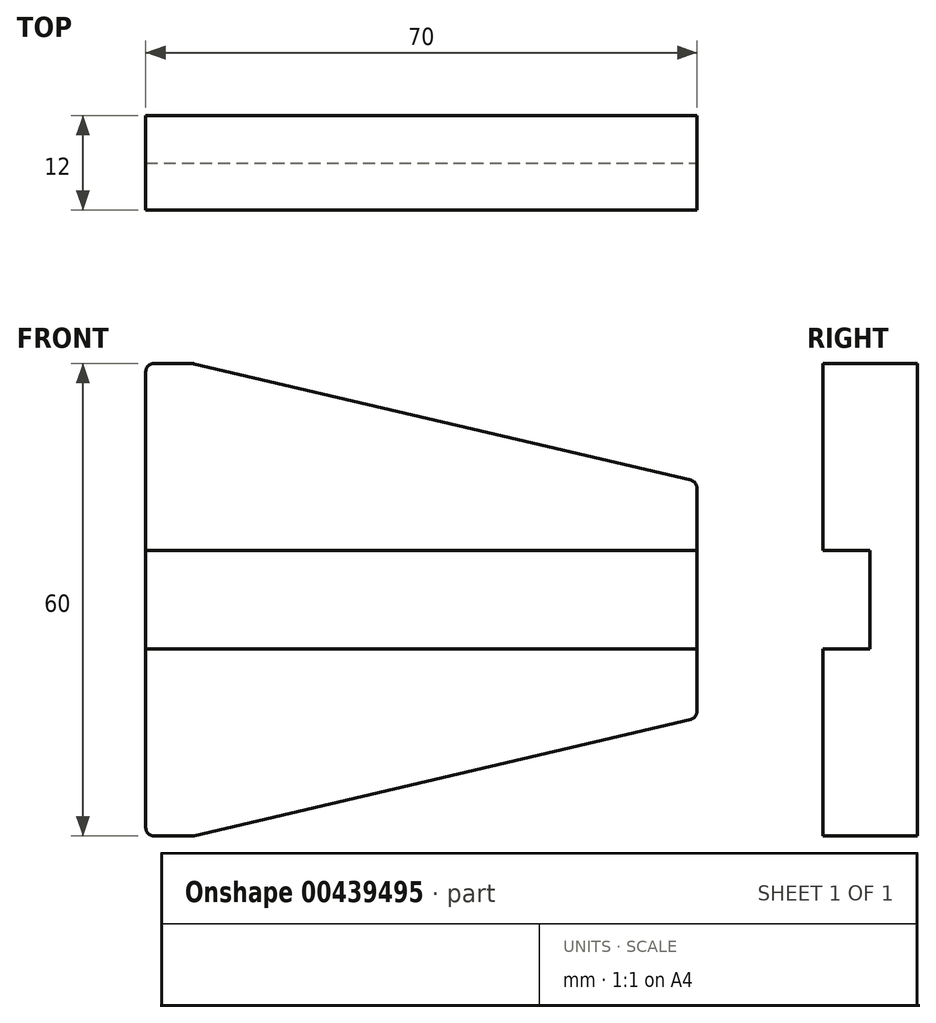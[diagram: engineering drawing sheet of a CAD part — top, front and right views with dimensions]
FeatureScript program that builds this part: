
annotation { "Feature Type Name" : "Feature", "Feature Type Description" : "" }
export const myFeature = defineFeature(function(context is Context, id is Id, definition is map)
    precondition{}
    {
        {
            var Q0;
            Q0=qCreatedBy(makeId("Front.planeOp"),FACE);
            var sketch = newSketch(context, id + "F0", { "sketchPlane" : qUnion([Q0])});
            skLineSegment(sketch, "E0", {"start": v(0, 30) * mm, "end": v(0, -30) * mm});
            skLineSegment(sketch, "E1", {"start": v(6, -30) * mm, "end": v(70, -15) * mm});
            skLineSegment(sketch, "E2", {"start": v(70, -15) * mm, "end": v(70, 15) * mm});
            skLineSegment(sketch, "E3", {"start": v(70, 15) * mm, "end": v(6, 30) * mm});
            skLineSegment(sketch, "E4", {"start": v(0, 30) * mm, "end": v(6, 30) * mm});
            skLineSegment(sketch, "E5", {"start": v(0, -30) * mm, "end": v(6, -30) * mm});
            skSolve(sketch);
        }
        {
            var Q0;
            Q0 = qSketchRegion(id + "F0", true);
            extrude(context, id + "F1", {"entities" : qUnion([Q0]), "depth" : 12 * mm, "offsetDistance" : 25 * mm});
        }
        {
            var Q0;
            Q0=makeQuery(id+"F1.opExtrude","SWEPT_FACE",FACE,{"disambiguationData":[OSD([sQuery(id+"F0.wireOp",EDGE,"E2")])]});
            var sketch = newSketch(context, id + "F2", { "sketchPlane" : qUnion([Q0])});
            skLineSegment(sketch, "E6.bottom", {"start": v(-12, 6.25) * mm, "end": v(-6, 6.25) * mm});
            skLineSegment(sketch, "E6.top", {"start": v(-12, -6.25) * mm, "end": v(-6, -6.25) * mm});
            skLineSegment(sketch, "E6.left", {"start": v(-12, 6.25) * mm, "end": v(-12, -6.25) * mm});
            skLineSegment(sketch, "E6.right", {"start": v(-6, 6.25) * mm, "end": v(-6, -6.25) * mm});
            skPoint(sketch, "E7", {"position": v(-12, 0) * mm});
            skPoint(sketch, "E7.positionSnap0", {"position": v(0, 0) * mm});
            skSolve(sketch);
        }
        {
            var Q0;
            Q0 = qSketchRegion(id + "F2", true);
            extrude(context, id + "F3", {"entities" : qUnion([Q0]), "operationType" : NewBodyOperationType.REMOVE, "endBound" : BoundingType.THROUGH_ALL, "oppositeDirection" : true, "depth" : 25 * mm, "offsetDistance" : 25 * mm});
        }
        {
            var Q0;
            Q0=makeQuery(id+"F1.opExtrude","SWEPT_EDGE",EDGE,{"disambiguationData":[OSD([sQuery(id+"F0.wireOp",EDGE,"E2"),sQuery(id+"F0.wireOp",EDGE,"E3")])]});
            var Q1;
            Q1=makeQuery(id+"F1.opExtrude","SWEPT_EDGE",EDGE,{"disambiguationData":[OSD([sQuery(id+"F0.wireOp",EDGE,"E3"),sQuery(id+"F0.wireOp",EDGE,"E4")])]});
            var Q2;
            Q2=makeQuery(id+"F1.opExtrude","SWEPT_EDGE",EDGE,{"disambiguationData":[OSD([sQuery(id+"F0.wireOp",EDGE,"E0"),sQuery(id+"F0.wireOp",EDGE,"E4")])]});
            var Q3;
            Q3=makeQuery(id+"F1.opExtrude","SWEPT_EDGE",EDGE,{"disambiguationData":[OSD([sQuery(id+"F0.wireOp",EDGE,"E1"),sQuery(id+"F0.wireOp",EDGE,"E2")])]});
            var Q4;
            Q4=makeQuery(id+"F1.opExtrude","SWEPT_EDGE",EDGE,{"disambiguationData":[OSD([sQuery(id+"F0.wireOp",EDGE,"E1"),sQuery(id+"F0.wireOp",EDGE,"E5")])]});
            var Q5;
            Q5=makeQuery(id+"F1.opExtrude","SWEPT_EDGE",EDGE,{"disambiguationData":[OSD([sQuery(id+"F0.wireOp",EDGE,"E0"),sQuery(id+"F0.wireOp",EDGE,"E5")])]});
            fillet(context, id + "F4", {"entities" : qUnion([Q0, Q1, Q2, Q3, Q4, Q5]), "radius" : 1 * mm, "tangentPropagation" : true, "allowEdgeOverflow" : false});
        }
    });
